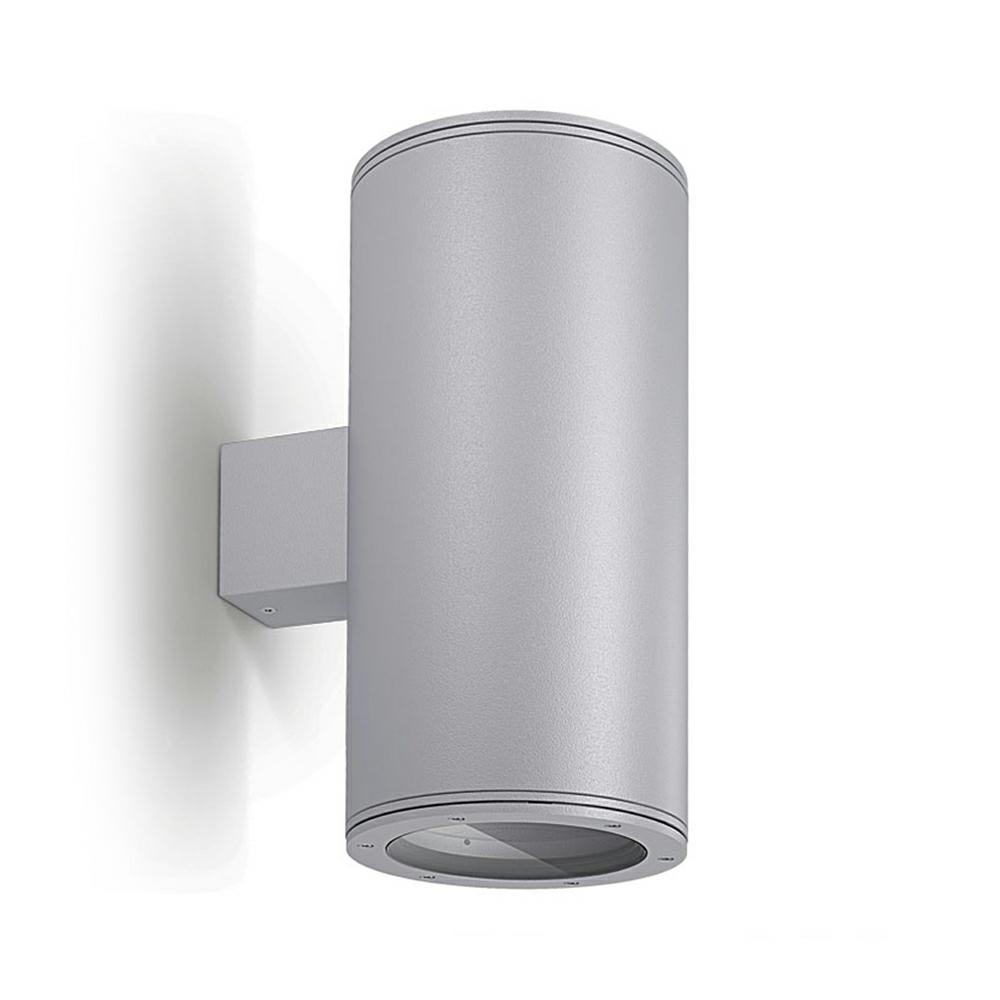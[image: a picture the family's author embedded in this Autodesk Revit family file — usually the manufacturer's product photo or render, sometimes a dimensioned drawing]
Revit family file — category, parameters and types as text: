
# Revit family: Platek_Monaco_200_Applique_1_Opening
name_source: partatom
category: Apparecchi per illuminazione
revit_build: Autodesk Revit 2018 (Build: 20170223_1515(x64)
units: mm (PartAtom-declared; Revit-internal decimal feet)

## family parameters
Basato su piano di lavoro = No
Condiviso = No
Punto di calcolo locali = No
Quota connettore circolare = Usa diametro
Sempre verticale = Sì
Sorgente d'illuminazione = Sì
Taglio con vuoti quando caricato = No
Tipo di parte = Normale

## types (2) — shared parameters
Angolo inclinazione = 90.00°
Body = PLK_06_Grey
CRI = >80
Colour Temprature = 3000 K
Commenti sul tipo = Facades, Wall
Descrizione = Outdoor Lighting, Wall mounted
Diffuse Type = Transparent Glass
Dimmable = NO
Emetti da diametro cerchio = 160 mm  [stored 0.524934 ft]
Energy Efficiency Rating = A/A+/A++
Filtro dei colori = 16777215
Frequency = 50/60 Hz
Glass = PLK_Light Source
IK Rating = IK10
IP Rating = IP65
Immagine tipo = monaco_200_applique.jpg
Inside Body = PLK_Optic
Insulation Class = 1
LED Protection = Surge protection included
Lampada = LED
Luminaire Wattage = 21 W
Manufacturer Comment = 1 Opening
Modello = Monaco 200 1Opening
Mounting Type = Wall
Nota chiave = Other LED colors available on request
Power Supply Unit = Included
Product Dimension = L280mm x L200mm x 400mm
Product Documentation Link = https://www.platek.eu
Product Page URL = https://www.platek.eu
Produttore = PLATEK SRL
Rendi la forma visibile nel rendering = No
Supply Voltage = 230 V
Supply Voltage Max = 240 V
Supply Voltage Min = 220 V
URL = www.platek.eu
Variazione temperatura colore lampada con luminosità attenuata = <Nessuno>

## per-type parameters (varying)
| type | Codice assieme | File diagramma fotometrico | Luminaire Luminous Flux | Luminaure Luminous Intensity | PLATEK Article Code |
| 8442411_21W_LED_3000K | 8442411.02(White);  8442411.06(Grey);  8442411.01(Black);  8442411.08(Anthracite); 8442411.07(Corten);  8442411.09(Bronze) | 8442411.IES | 1935 lm | 39086 cd | 8442411 |
| 8442418_21W_LED_3000K | 8442418.02(White);  8442418.06(Grey);  8442418.01(Black);  8442418.08(Anthracite); 8442418.07(Corten);  8442418.09(Bronze) | 8442418.IES | 1615 lm | 2223 cd | 8442418 |

note: [stored X ft] marks values corroborated as IEEE doubles in the binary element streams (Revit-internal decimal feet)
